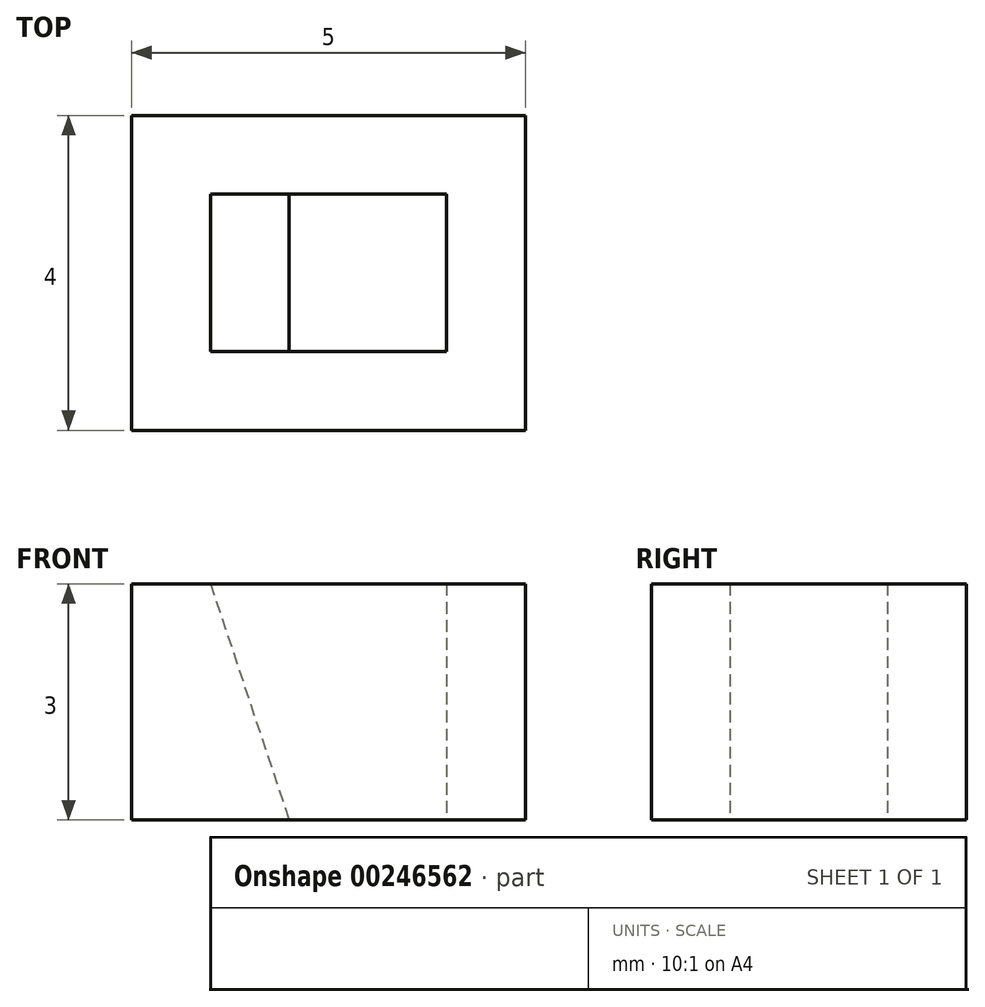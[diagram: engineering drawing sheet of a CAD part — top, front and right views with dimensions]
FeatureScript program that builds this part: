
annotation { "Feature Type Name" : "Feature", "Feature Type Description" : "" }
export const myFeature = defineFeature(function(context is Context, id is Id, definition is map)
    precondition{}
    {
        {
            var Q0;
            Q0=qCreatedBy(makeId("Top.planeOp"),FACE);
            var sketch = newSketch(context, id + "F0", { "sketchPlane" : qUnion([Q0])});
            skLineSegment(sketch, "E0.bottom", {"start": v(0, 0) * mm, "end": v(5, 0) * mm});
            skLineSegment(sketch, "E0.top", {"start": v(0, 4) * mm, "end": v(5, 4) * mm});
            skLineSegment(sketch, "E0.left", {"start": v(0, 0) * mm, "end": v(0, 4) * mm});
            skLineSegment(sketch, "E0.right", {"start": v(5, 0) * mm, "end": v(5, 4) * mm});
            skSolve(sketch);
        }
        {
            var Q0;
            Q0=makeQuery(id+"F0.imprint","IMPRINT",FACE,{"disambiguationData":[TD([[makeQuery(id+"F0.imprint","IMPRINT",EDGE,{"derivedFrom":sQuery(id+"F0.wireOp",EDGE,"E0.bottom")}),1.0]])]});
            extrude(context, id + "F1", {"entities" : qUnion([Q0]), "depth" : 3 * mm});
        }
        {
            var Q0;
            Q0=makeQuery(id+"F1.opExtrude","CAP_FACE",FACE,{"disambiguationData":[OSD([sQuery(id+"F0.wireOp",EDGE,"E0.bottom"),sQuery(id+"F0.wireOp",EDGE,"E0.top"),sQuery(id+"F0.wireOp",EDGE,"E0.left"),sQuery(id+"F0.wireOp",EDGE,"E0.right")])],"isStart":true});
            var sketch = newSketch(context, id + "F2", { "sketchPlane" : qUnion([Q0])});
            skLineSegment(sketch, "E1.bottom", {"start": v(2, -1) * mm, "end": v(4, -1) * mm});
            skLineSegment(sketch, "E1.top", {"start": v(2, -3) * mm, "end": v(4, -3) * mm});
            skLineSegment(sketch, "E1.left", {"start": v(2, -1) * mm, "end": v(2, -3) * mm});
            skLineSegment(sketch, "E1.right", {"start": v(4, -1) * mm, "end": v(4, -3) * mm});
            skSolve(sketch);
        }
        {
            var Q0;
            Q0=makeQuery(id+"F1.opExtrude","CAP_FACE",FACE,{"disambiguationData":[OSD([sQuery(id+"F0.wireOp",EDGE,"E0.bottom"),sQuery(id+"F0.wireOp",EDGE,"E0.top"),sQuery(id+"F0.wireOp",EDGE,"E0.left"),sQuery(id+"F0.wireOp",EDGE,"E0.right")])],"isStart":false});
            var sketch = newSketch(context, id + "F3", { "sketchPlane" : qUnion([Q0])});
            skLineSegment(sketch, "E2.left", {"start": v(0, 3) * mm, "end": v(0, 1) * mm});
            skLineSegment(sketch, "E3.bottom", {"start": v(1, 3) * mm, "end": v(4, 3) * mm});
            skLineSegment(sketch, "E3.top", {"start": v(1, 1) * mm, "end": v(4, 1) * mm});
            skLineSegment(sketch, "E3.left", {"start": v(1, 3) * mm, "end": v(1, 1) * mm});
            skLineSegment(sketch, "E3.right", {"start": v(4, 3) * mm, "end": v(4, 1) * mm});
            skSolve(sketch);
        }
        {
            var Q1;
            Q1=makeQuery(id+"F3.imprint","IMPRINT",FACE,{"disambiguationData":[TD([[makeQuery(id+"F3.imprint","IMPRINT",EDGE,{"derivedFrom":sQuery(id+"F3.wireOp",EDGE,"E3.bottom")}),-1.0]])]});
            var Q2;
            Q2=makeQuery(id+"F2.imprint","IMPRINT",FACE,{"disambiguationData":[TD([[makeQuery(id+"F2.imprint","IMPRINT",EDGE,{"derivedFrom":sQuery(id+"F2.wireOp",EDGE,"E1.bottom")}),-1.0]])]});
            loft(context, id + "F4", {"operationType" : NewBodyOperationType.REMOVE, "sheetProfilesArray" : [{ "sheetProfileEntities" : qUnion([Q1]) }, { "sheetProfileEntities" : qUnion([Q2]) }]});
        }
    });
